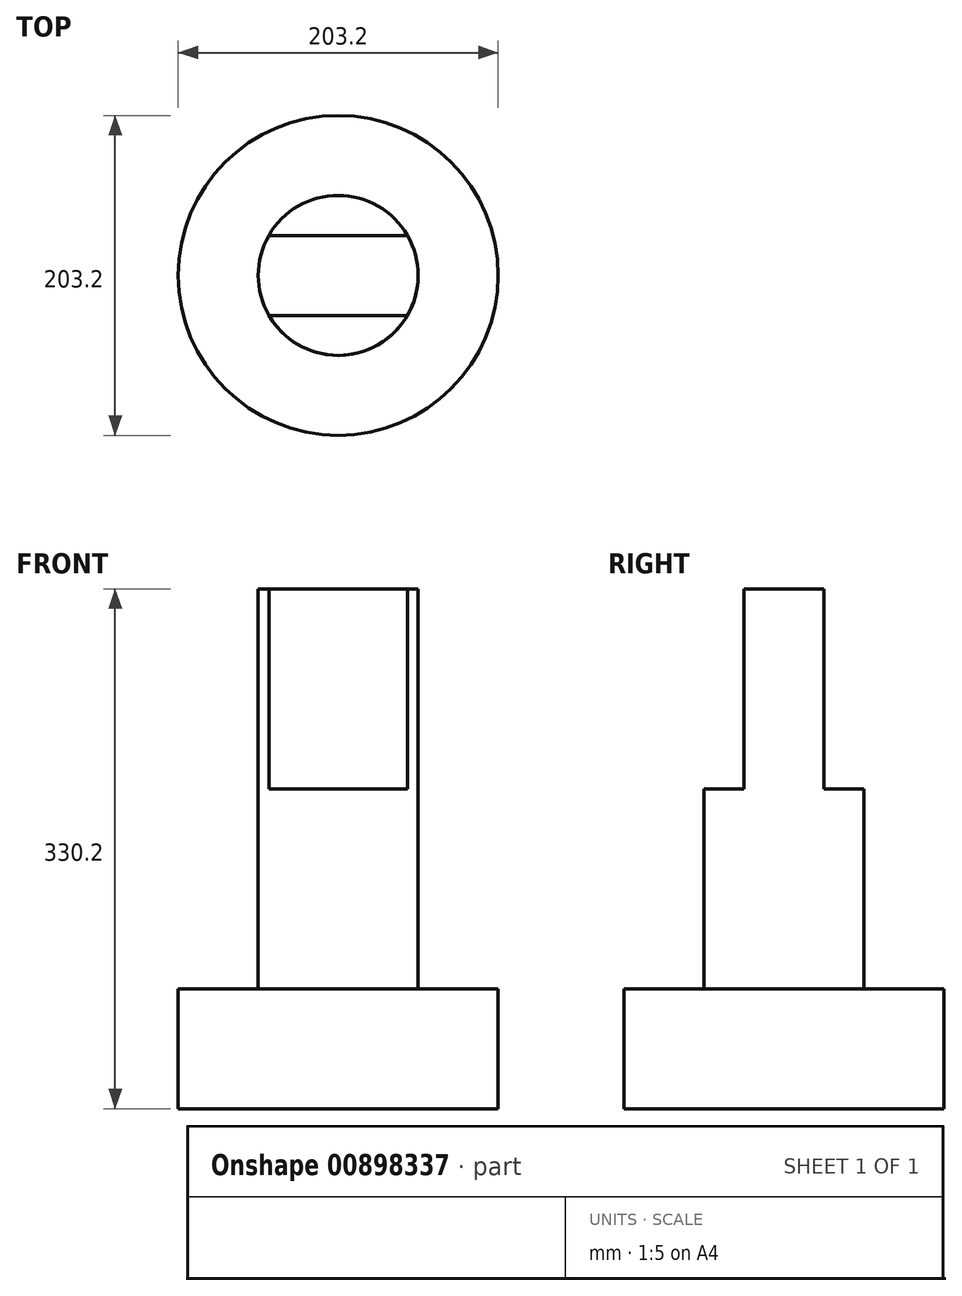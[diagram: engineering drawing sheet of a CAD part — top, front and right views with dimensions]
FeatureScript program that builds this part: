
annotation { "Feature Type Name" : "Feature", "Feature Type Description" : "" }
export const myFeature = defineFeature(function(context is Context, id is Id, definition is map)
    precondition{}
    {
        {
            var Q0;
            Q0=qCreatedBy(makeId("Top.planeOp"),FACE);
            var sketch = newSketch(context, id + "F0", { "sketchPlane" : qUnion([Q0])});
            skCircle(sketch, "E0", {"center": v(0, 0) * mm, "radius": 101.6 * mm});
            skSolve(sketch);
        }
        {
            var Q0;
            Q0=makeQuery(id+"F0.imprint","IMPRINT",FACE,{"disambiguationData":[TD([[makeQuery(id+"F0.imprint","IMPRINT",EDGE,{"derivedFrom":sQuery(id+"F0.wireOp",EDGE,"E0")}),1.0]])]});
            extrude(context, id + "F1", {"entities" : qUnion([Q0]), "depth" : 76.2 * mm, "offsetDistance" : 25.4 * mm});
        }
        {
            var Q0;
            Q0=makeQuery(id+"F1.opExtrude","CAP_FACE",FACE,{"disambiguationData":[OSD([sQuery(id+"F0.wireOp",EDGE,"E0")])],"isStart":false});
            var sketch = newSketch(context, id + "F2", { "sketchPlane" : qUnion([Q0])});
            skCircle(sketch, "E1", {"center": v(0, 0) * mm, "radius": 50.8 * mm});
            skSolve(sketch);
        }
        {
            var Q0;
            Q0=makeQuery(id+"F2.imprint","IMPRINT",FACE,{"disambiguationData":[TD([[makeQuery(id+"F2.imprint","IMPRINT",EDGE,{"derivedFrom":sQuery(id+"F2.wireOp",EDGE,"E1")}),1.0]])]});
            extrude(context, id + "F3", {"entities" : qUnion([Q0]), "operationType" : NewBodyOperationType.ADD, "depth" : 127 * mm, "offsetDistance" : 25.4 * mm});
        }
        {
            var Q0;
            Q0=makeQuery(id+"F3.opExtrude","CAP_FACE",FACE,{"disambiguationData":[OSD([sQuery(id+"F2.wireOp",EDGE,"E1")])],"isStart":false});
            var sketch = newSketch(context, id + "F4", { "sketchPlane" : qUnion([Q0])});
            skLineSegment(sketch, "E2", {"start": v(-44, 25.4) * mm, "end": v(44, 25.4) * mm});
            skLineSegment(sketch, "E3", {"start": v(-44, -25.4) * mm, "end": v(44, -25.4) * mm});
            skSolve(sketch);
        }
        {
            var Q0;
            {var subQ0=sQuery(id+"F4.wireOp",EDGE,"E2");Q0=makeQuery(id+"F4.imprint","IMPRINT",FACE,{"disambiguationData":[TD([[makeQuery(id+"F4.imprint","IMPRINT",EDGE,{"derivedFrom":subQ0}),-1.0]])]});}
            extrude(context, id + "F5", {"entities" : qUnion([Q0]), "operationType" : NewBodyOperationType.ADD, "depth" : 127 * mm, "offsetDistance" : 25.4 * mm});
        }
    });
